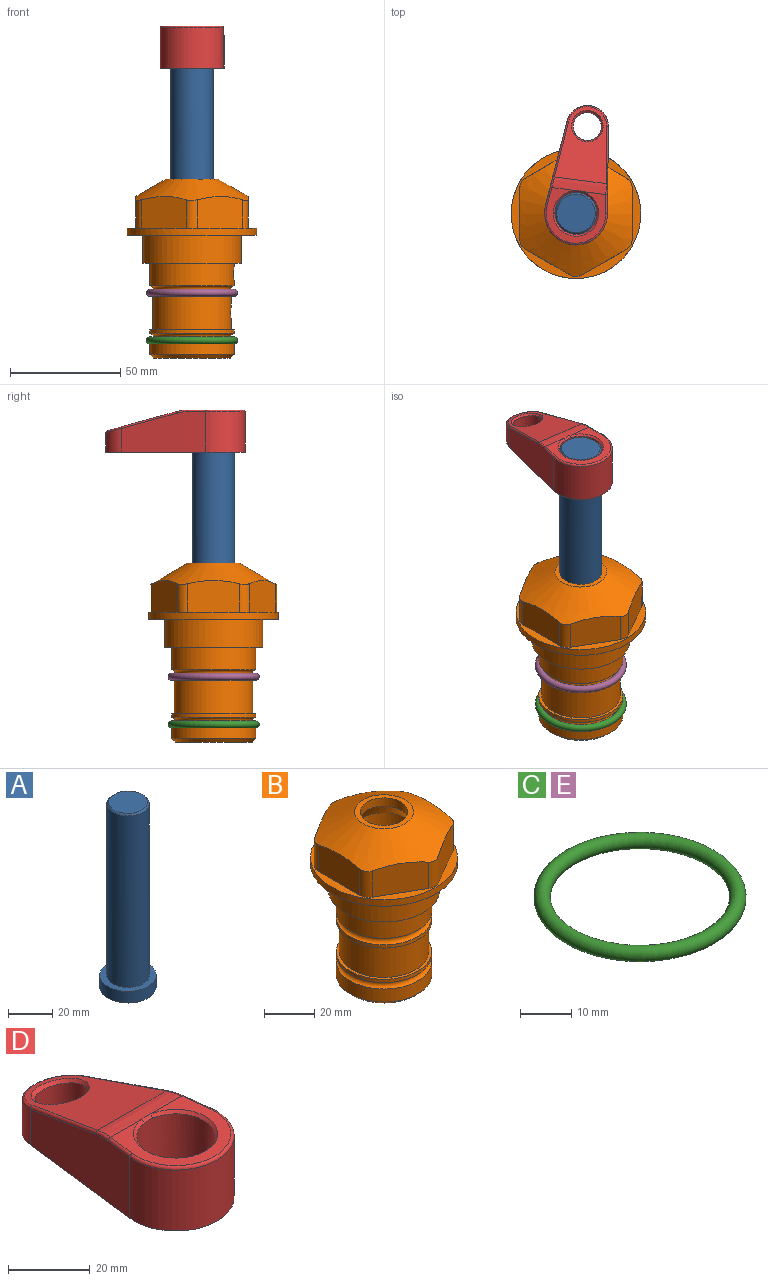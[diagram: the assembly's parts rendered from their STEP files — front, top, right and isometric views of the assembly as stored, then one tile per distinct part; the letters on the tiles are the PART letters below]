
ASSEMBLY  parts=5 mates=3
PART A: 6 faces, bbox 25.4x25.4x101.6 mm
  f0: plane 17.46x17.46mm, normal (0,0,1), area 239.5mm2, adj f5
  f1: plane 25.4x25.4mm, normal (0,0,-1), area 506.7mm2, adj f2
  f2: cylinder r=12.7mm len=25.4mm, axis (0,0,1), area 506.7mm2, adj f1,f3
  f3: plane 25.4x25.4mm, normal (0,0,1), area 221.7mm2, adj f2,f4
  f4: cylinder r=9.53mm len=94.46mm, axis (0,0,1), area 5653mm2, adj f3,f5
  f5: cone r=8.73mm half-angle=45deg, axis (0,0,-1), area 64.4mm2, adj f0,f4
PART B: 36 faces, bbox 58.7x58.7x81 mm
  f0: cylinder r=17.78mm len=35.56mm, axis (0,0,1), area 1670.8mm2, adj f23,f24,f31
  f1: cylinder r=19.05mm len=38.1mm, axis (0,0,1), area 1191.9mm2, adj f26,f27,f30
  f2: plane 58.66x58.66mm, normal (0,0,-1), area 1150.6mm2, adj f3,f28
  f3: cylinder r=29.33mm len=58.66mm, axis (0,0,-1), area 585.1mm2, adj f2,f4
  f4: plane 58.66x58.66mm, normal (0,0,1), area 475.9mm2, adj f3,f5,f6,f7,f8,f9,f10,f11
  f5: plane 20.32x14.34mm, normal (-0.5,0.87,0), area 324.4mm2, adj f4,f15,f16,f17
  f6: plane 20.32x14.34mm, normal (0.5,0.87,0), area 324.4mm2, adj f4,f14,f15,f17
  f7: plane 23.48x14.34mm, normal (1,0,0), area 324.4mm2, adj f4,f13,f14,f17
  f8: plane 20.32x14.34mm, normal (0.5,-0.87,0), area 324.4mm2, adj f4,f12,f13,f17
  f9: plane 20.32x14.34mm, normal (-0.5,-0.87,0), area 324.4mm2, adj f4,f11,f12,f17
  f10: plane 23.48x14.34mm, normal (-1,0,0), area 324.4mm2, adj f4,f11,f16,f17
  f11: cylinder r=5.08mm len=12.85mm, axis (0,0,-1), area 67.2mm2, adj f4,f9,f10,f17
  f12: cylinder r=5.08mm len=12.85mm, axis (0,0,-1), area 67.2mm2, adj f4,f8,f9,f17
  f13: cylinder r=5.08mm len=12.85mm, axis (0,0,-1), area 67.2mm2, adj f4,f7,f8,f17
  f14: cylinder r=5.08mm len=12.85mm, axis (0,0,-1), area 67.2mm2, adj f4,f6,f7,f17
  f15: cylinder r=5.08mm len=12.85mm, axis (0,0,-1), area 67.2mm2, adj f4,f5,f6,f17
  f16: cylinder r=5.08mm len=12.85mm, axis (0,0,-1), area 67.2mm2, adj f4,f5,f10,f17
  f17: cone r=11.73mm half-angle=60deg, axis (0,0,-1), area 2071.8mm2, adj f5,f6,f7,f8,f9,f10,f11,f12
  f18: plane 23.46x23.46mm, normal (0,0,1), area 147.4mm2, adj f17,f35
  f19: plane 34.93x34.93mm, normal (0,0,-1), area 958mm2, adj f29
  f20: cylinder r=19.05mm len=38.1mm, axis (0,0,1), area 760.1mm2, adj f21,f29
  f21: torus R=19.05mm, axis (0,0,1), area 565.3mm2, adj f20,f22
  f22: cylinder r=19.05mm len=38.1mm, axis (0,0,1), area 190mm2, adj f21,f23
  f23: plane 38.1x38.1mm, normal (0,0,1), area 146.9mm2, adj f0,f22
  f24: plane 38.1x38.1mm, normal (0,0,-1), area 146.9mm2, adj f0,f25
  f25: cylinder r=19.05mm len=38.1mm, axis (0,0,1), area 190mm2, adj f24,f26
  f26: torus R=19.05mm, axis (0,0,1), area 565.3mm2, adj f1,f25
  f27: plane 44.45x44.45mm, normal (0,0,-1), area 411.7mm2, adj f1,f28
  f28: cylinder r=22.23mm len=44.45mm, axis (0,0,1), area 1773.5mm2, adj f2,f27
  f29: cone r=19.05mm half-angle=45deg, axis (0,0,1), area 257.5mm2, adj f19,f20
  f30: cylinder r=3.17mm len=6.75mm, axis (-1,0,0), area 128mm2, adj f1,f33
  f31: cylinder r=3.17mm len=6.35mm, axis (-1,0,0), area 102.5mm2, adj f0,f33
  f32: plane 25.4x25.4mm, normal (0,0,1), area 506.7mm2, adj f33
  f33: cylinder r=12.7mm len=66.42mm, axis (0,0,-1), area 5236.2mm2, adj f30,f31,f32,f34
  f34: cone r=9.53mm half-angle=30deg, axis (0,0,-1), area 443.4mm2, adj f33,f35
  f35: cylinder r=9.53mm len=19.05mm, axis (0,0,-1), area 240.9mm2, adj f18,f34
PART C: 1 faces, bbox 44.7x44.7x3.2 mm
  f0: torus R=19.05mm, axis (0,0,1), area 1193.9mm2
PART D: 31 faces, bbox 31.7x65.5x19.8 mm
  f0: plane 39.12x18.26mm, normal (0.99,0.12,0), area 612.2mm2, adj f1,f4,f7,f11,f13,f15
  f1: cylinder r=9.53mm len=18.91mm, axis (0,0,-1), area 296.1mm2, adj f0,f2,f7,f17
  f2: plane 39.12x18.26mm, normal (-0.99,0.12,0), area 612.2mm2, adj f1,f4,f7,f12,f14,f16
  f3: cylinder r=6.35mm len=12.7mm, axis (0,0,-1), area 362.4mm2, adj f7,f18
  f4: cylinder r=14.29mm len=28.58mm, axis (0,0,-1), area 882.2mm2, adj f0,f2,f7,f10
  f5: cylinder r=9.53mm len=19.05mm, axis (0,0,-1), area 1092.6mm2, adj f7,f19,f20
  f6: plane 26.99x23.69mm, normal (0,0,1), area 216.2mm2, adj f9,f10,f11,f12,f19
  f7: plane 63.5x28.58mm, normal (0,0,-1), area 661.8mm2, adj f0,f1,f2,f3,f4,f5,f22,f23
  f8: plane 33.52x23.6mm, normal (0,0.26,0.97), area 486mm2, adj f9,f15,f16,f17,f18
  f9: cylinder r=19.05mm len=24.72mm, axis (1,0,0), area 120.4mm2, adj f6,f8,f13,f14,f20
  f10: torus R=13.49mm, axis (0,0,1), area 59mm2, adj f4,f6,f11,f12
  f11: cylinder r=0.79mm len=8.67mm, axis (0.12,-0.99,0), area 10.8mm2, adj f0,f6,f10,f13
  f12: cylinder r=0.79mm len=8.67mm, axis (0.12,0.99,0), area 10.8mm2, adj f2,f6,f10,f14
  f13: bspline ~4.95x1.42mm, area 6.1mm2, adj f0,f9,f11,f15
  f14: bspline ~4.95x1.42mm, area 6.1mm2, adj f2,f9,f12,f16
  f15: cylinder r=0.79mm len=25.95mm, axis (0.12,-0.96,0.26), area 32.9mm2, adj f0,f8,f13,f17
  f16: cylinder r=0.79mm len=25.95mm, axis (0.12,0.96,-0.26), area 32.9mm2, adj f2,f8,f14,f17
  f17: bspline ~18.91x8.38mm, area 30mm2, adj f1,f8,f15,f16
  f18: bspline ~14.29x14.29mm, area 48.3mm2, adj f3,f8
  f19: cone r=9.53mm half-angle=45deg, axis (0,0,1), area 66.5mm2, adj f5,f6,f20
  f20: bspline ~3.22x0.96mm, area 3.5mm2, adj f5,f9,f19
  f21: plane 2.75x2.72mm, normal (0,0,-1), area 2.9mm2, adj f23,f25,f28
  f22: plane 23.05x15.88mm, normal (-0.99,-0.12,0), area 323.6mm2, adj f7,f25,f26,f27,f28,f29
  f23: plane 23.05x15.88mm, normal (0.99,-0.12,0), area 323.6mm2, adj f7,f21,f25,f27,f28,f30
  f24: cylinder r=9.53mm len=10.69mm, axis (0,0,-1), area 114.7mm2, adj f7,f27,f29,f30
  f25: cylinder r=12.7mm len=20.59mm, axis (0,0,-1), area 381.1mm2, adj f7,f21,f22,f23,f26,f28
  f26: plane 2.75x2.72mm, normal (0,0,-1), area 2.9mm2, adj f22,f25,f28
  f27: plane 19.72x18.37mm, normal (0,-0.26,-0.97), area 291.8mm2, adj f22,f23,f24,f28,f29,f30
  f28: cylinder r=15.88mm len=19.92mm, axis (1,0,0), area 54.8mm2, adj f21,f22,f23,f25,f26,f27
  f29: cylinder r=1.59mm len=11mm, axis (0,0,-1), area 34.7mm2, adj f7,f22,f24,f27
  f30: cylinder r=1.59mm len=11mm, axis (0,0,-1), area 34.7mm2, adj f7,f23,f24,f27
PART E: same geometry as C
PLACE A rot(axis=(0,0,-1),7.4deg) t=(0,0,30.41)mm
PLACE B at identity fixed
PLACE C t=(0,0,-23.18)mm
PLACE D rot(axis=(0,0,-1),7.4deg) t=(0,0,31.21)mm
PLACE E t=(0,0,-1.59)mm
MATE fastened C.f0 <-> B.f0  axis (0,0,1) through (0,0,-47.69)mm
MATE fastened A.f2 <-> D.f4  axis (0,0,1) through (0,0,93.91)mm
MATE cylindrical A.f2 <-> B.f0  axis (0,0,-1) through (0,0,-7.69)mm
